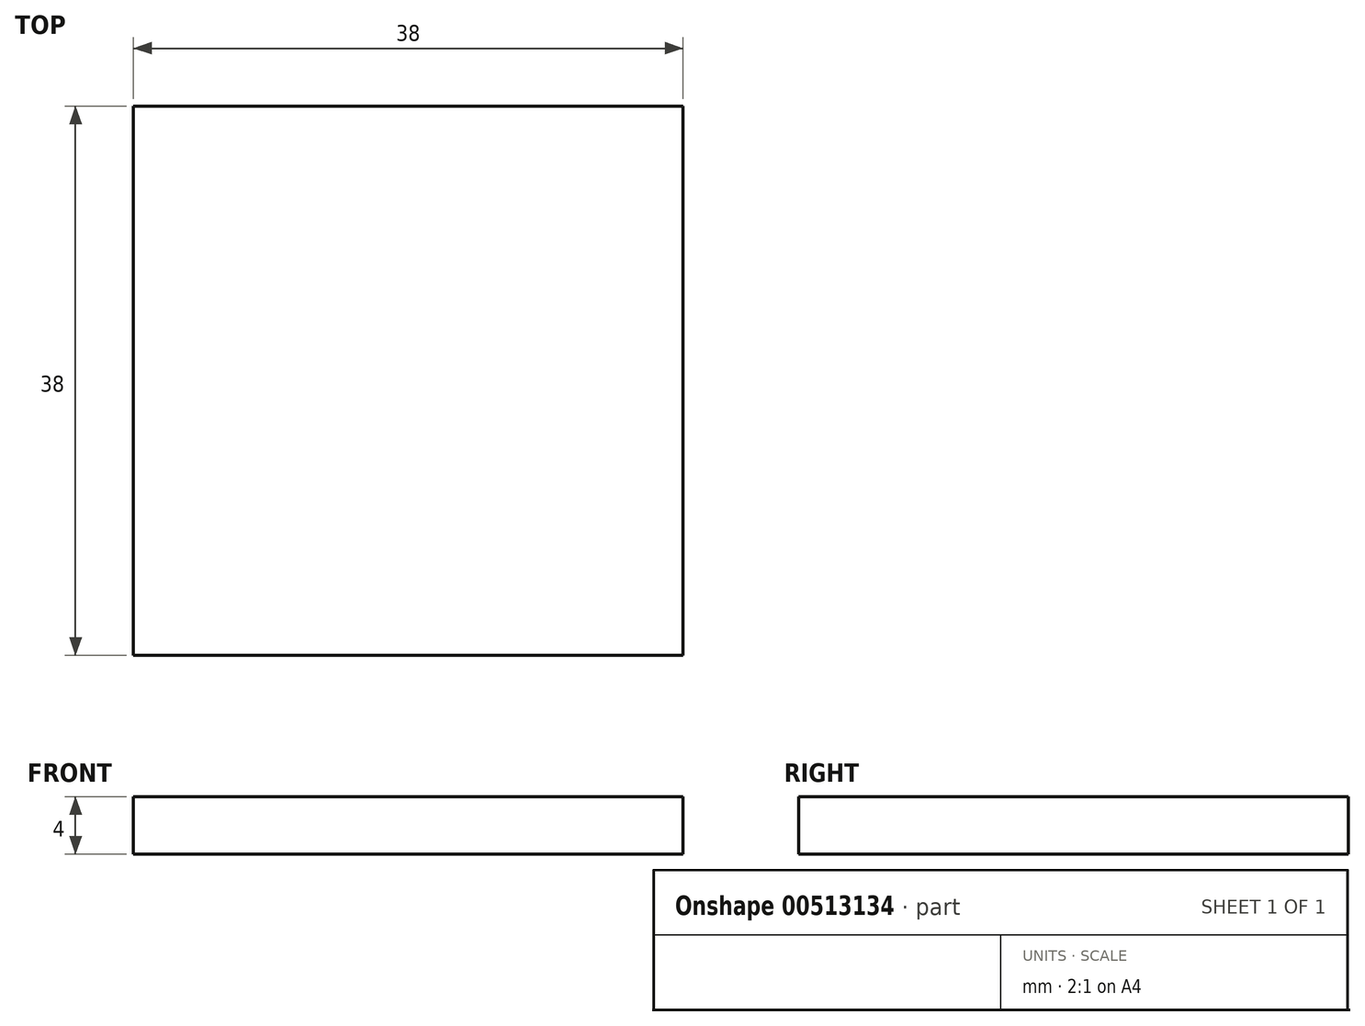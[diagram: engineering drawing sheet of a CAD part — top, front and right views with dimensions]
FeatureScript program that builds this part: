
annotation { "Feature Type Name" : "Feature", "Feature Type Description" : "" }
export const myFeature = defineFeature(function(context is Context, id is Id, definition is map)
    precondition{}
    {
        {
            var Q0;
            Q0=qCreatedBy(makeId("Top.planeOp"),FACE);
            var sketch = newSketch(context, id + "F0", { "sketchPlane" : qUnion([Q0])});
            skLineSegment(sketch, "E0", {"start": v(0, 0) * mm, "end": v(-38, 0) * mm});
            skLineSegment(sketch, "E1", {"start": v(-38, 0) * mm, "end": v(-38, 38) * mm});
            skLineSegment(sketch, "E2", {"start": v(-38, 38) * mm, "end": v(0, 38) * mm});
            skLineSegment(sketch, "E3", {"start": v(0, 38) * mm, "end": v(0, 0) * mm});
            skSolve(sketch);
        }
        {
            var Q0;
            Q0=makeQuery(id+"F0.imprint","IMPRINT",FACE,{"disambiguationData":[TD([[makeQuery(id+"F0.imprint","IMPRINT",EDGE,{"derivedFrom":sQuery(id+"F0.wireOp",EDGE,"E0")}),-1.0]])]});
            extrude(context, id + "F1", {"entities" : qUnion([Q0]), "offsetDistance" : 25 * mm, "depth" : 4 * mm});
        }
    });
